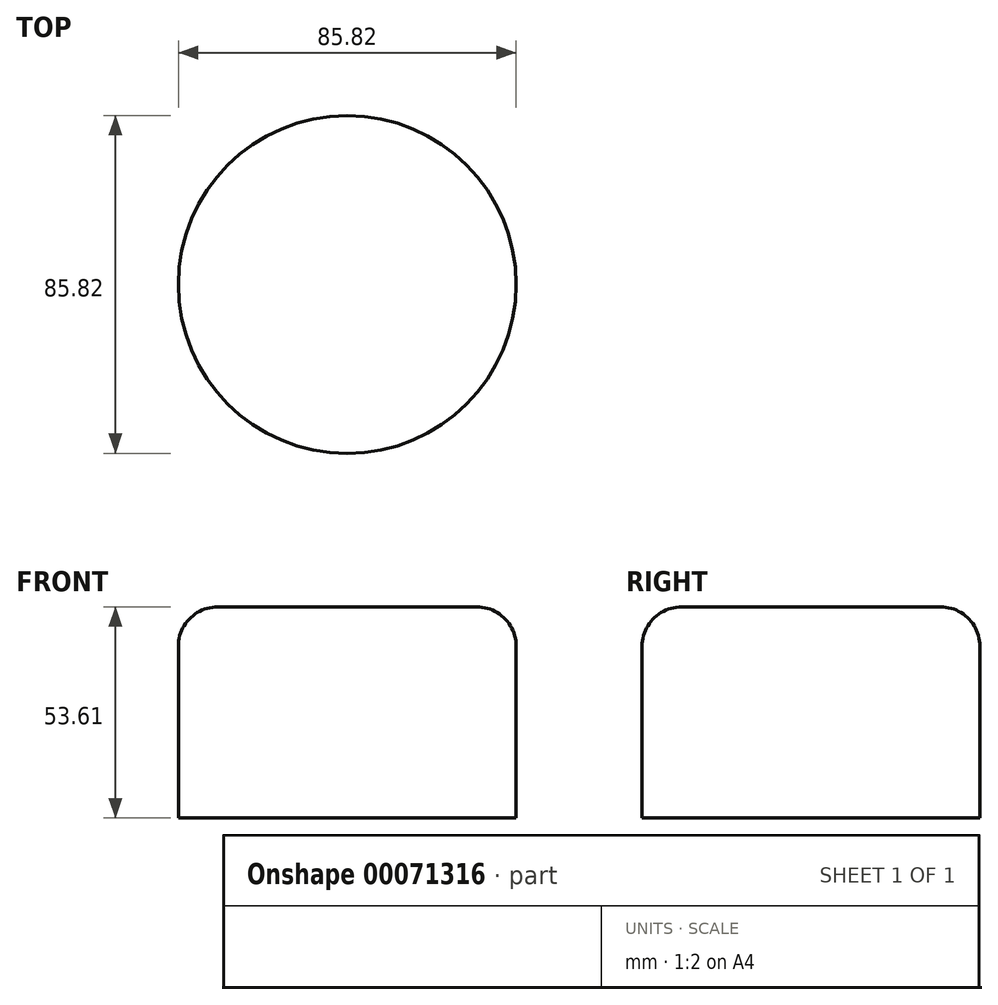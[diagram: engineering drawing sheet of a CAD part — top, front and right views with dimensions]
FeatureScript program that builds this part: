
annotation { "Feature Type Name" : "Feature", "Feature Type Description" : "" }
export const myFeature = defineFeature(function(context is Context, id is Id, definition is map)
    precondition{}
    {
        {
            var Q0;
            Q0=qCreatedBy(makeId("Top.planeOp"),FACE);
            var sketch = newSketch(context, id + "F0", { "sketchPlane" : qUnion([Q0])});
            skCircle(sketch, "E0", {"center": v(0, 0) * mm, "radius": 42.91 * mm});
            skSolve(sketch);
        }
        {
            var Q0;
            Q0=makeQuery(id+"F0.imprint","IMPRINT",FACE,{"disambiguationData":[TD([[makeQuery(id+"F0.imprint","IMPRINT",EDGE,{"derivedFrom":sQuery(id+"F0.wireOp",EDGE,"E0")}),1.0]])]});
            extrude(context, id + "F1", {"entities" : qUnion([Q0]), "depth" : 53.6 * mm});
        }
        {
            var Q0;
            Q0=makeQuery(id+"F1.opExtrude","CAP_EDGE",EDGE,{"disambiguationData":[OSD([sQuery(id+"F0.wireOp",EDGE,"E0")])],"isStart":false});
            var Q1;
            Q1=makeQuery(id+"F1.opExtrude","CAP_FACE",FACE,{"disambiguationData":[OSD([sQuery(id+"F0.wireOp",EDGE,"E0")])],"isStart":false});
            fillet(context, id + "F2", {"entities" : qUnion([Q0, Q1]), "radius" : 10 * mm, "tangentPropagation" : true, "allowEdgeOverflow" : false});
        }
    });
